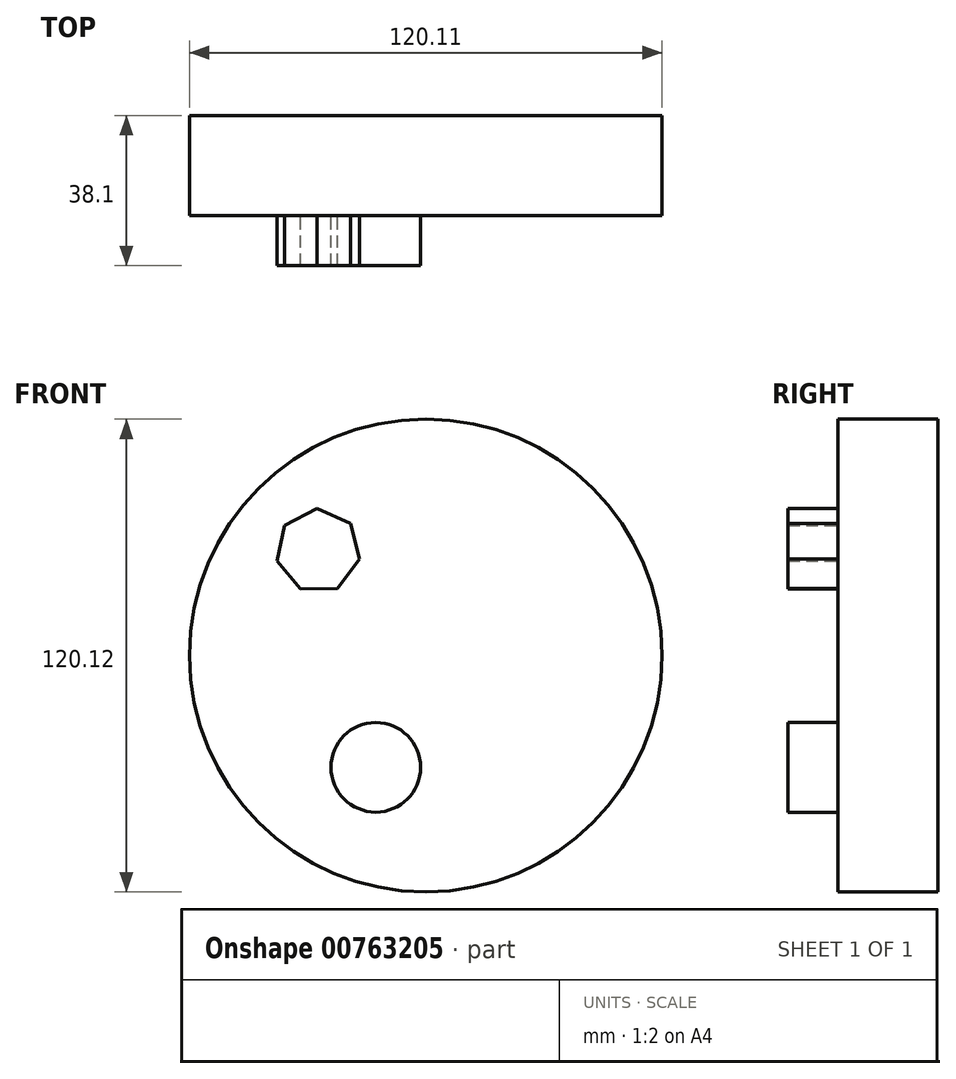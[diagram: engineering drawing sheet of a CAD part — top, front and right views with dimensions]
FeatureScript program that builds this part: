
annotation { "Feature Type Name" : "Feature", "Feature Type Description" : "" }
export const myFeature = defineFeature(function(context is Context, id is Id, definition is map)
    precondition{}
    {
        {
            var Q0;
            Q0=qCreatedBy(makeId("Front.planeOp"),FACE);
            var sketch = newSketch(context, id + "F0", { "sketchPlane" : qUnion([Q0])});
            skCircle(sketch, "E0", {"center": v(-50.62, 0) * mm, "radius": 60.06 * mm});
            skSolve(sketch);
        }
        {
            var Q0;
            Q0=makeQuery(id+"F0.imprint","IMPRINT",FACE,{"disambiguationData":[TD([[makeQuery(id+"F0.imprint","IMPRINT",EDGE,{"derivedFrom":sQuery(id+"F0.wireOp",EDGE,"E0")}),1.0]])]});
            extrude(context, id + "F1", {"entities" : qUnion([Q0]), "depth" : 25.4 * mm, "offsetDistance" : 25.4 * mm});
        }
        {
            var Q0;
            Q0=makeQuery(id+"F1.opExtrude","CAP_FACE",FACE,{"disambiguationData":[OSD([sQuery(id+"F0.wireOp",EDGE,"E0")])],"isStart":false});
            var sketch = newSketch(context, id + "F2", { "sketchPlane" : qUnion([Q0])});
            skCircle(sketch, "E1.cCircle", {"center": v(-78, 26.62) * mm, "radius": 9.67 * mm, "construction": true});
            skLineSegment(sketch, "E1.0", {"start": v(-67.48, 24.5) * mm, "end": v(-73.1, 17.07) * mm});
            skLineSegment(sketch, "E1.1", {"start": v(-73.1, 17.07) * mm, "end": v(-82.4, 16.84) * mm});
            skLineSegment(sketch, "E1.2", {"start": v(-82.4, 16.84) * mm, "end": v(-88.4, 23.97) * mm});
            skLineSegment(sketch, "E1.3", {"start": v(-88.4, 23.97) * mm, "end": v(-86.55, 33.1) * mm});
            skLineSegment(sketch, "E1.4", {"start": v(-86.55, 33.1) * mm, "end": v(-78.27, 37.34) * mm});
            skLineSegment(sketch, "E1.5", {"start": v(-78.27, 37.34) * mm, "end": v(-69.78, 33.52) * mm});
            skLineSegment(sketch, "E1.6", {"start": v(-69.78, 33.52) * mm, "end": v(-67.48, 24.5) * mm});
            skPoint(sketch, "E1.0.midPoint", {"position": v(-70.3, 20.79) * mm});
            skSolve(sketch);
        }
        {
            var Q0;
            Q0=makeQuery(id+"F2.imprint","IMPRINT",FACE,{"disambiguationData":[TD([[makeQuery(id+"F2.imprint","IMPRINT",EDGE,{"derivedFrom":sQuery(id+"F2.wireOp",EDGE,"E1.0")}),-1.0]])]});
            extrude(context, id + "F3", {"entities" : qUnion([Q0]), "operationType" : NewBodyOperationType.ADD, "depth" : 12.7 * mm, "offsetDistance" : 25.4 * mm});
        }
        {
            var Q0;
            Q0=makeQuery(id+"F1.opExtrude","CAP_FACE",FACE,{"disambiguationData":[OSD([sQuery(id+"F0.wireOp",EDGE,"E0")])],"isStart":false});
            var sketch = newSketch(context, id + "F4", { "sketchPlane" : qUnion([Q0])});
            skCircle(sketch, "E2", {"center": v(-63.33, -28.42) * mm, "radius": 11.39 * mm});
            skSolve(sketch);
        }
        {
            var Q0;
            Q0=makeQuery(id+"F4.imprint","IMPRINT",FACE,{"disambiguationData":[TD([[makeQuery(id+"F4.imprint","IMPRINT",EDGE,{"derivedFrom":sQuery(id+"F4.wireOp",EDGE,"E2")}),1.0]])]});
            extrude(context, id + "F5", {"entities" : qUnion([Q0]), "operationType" : NewBodyOperationType.ADD, "depth" : 12.7 * mm, "offsetDistance" : 25.4 * mm});
        }
    });
